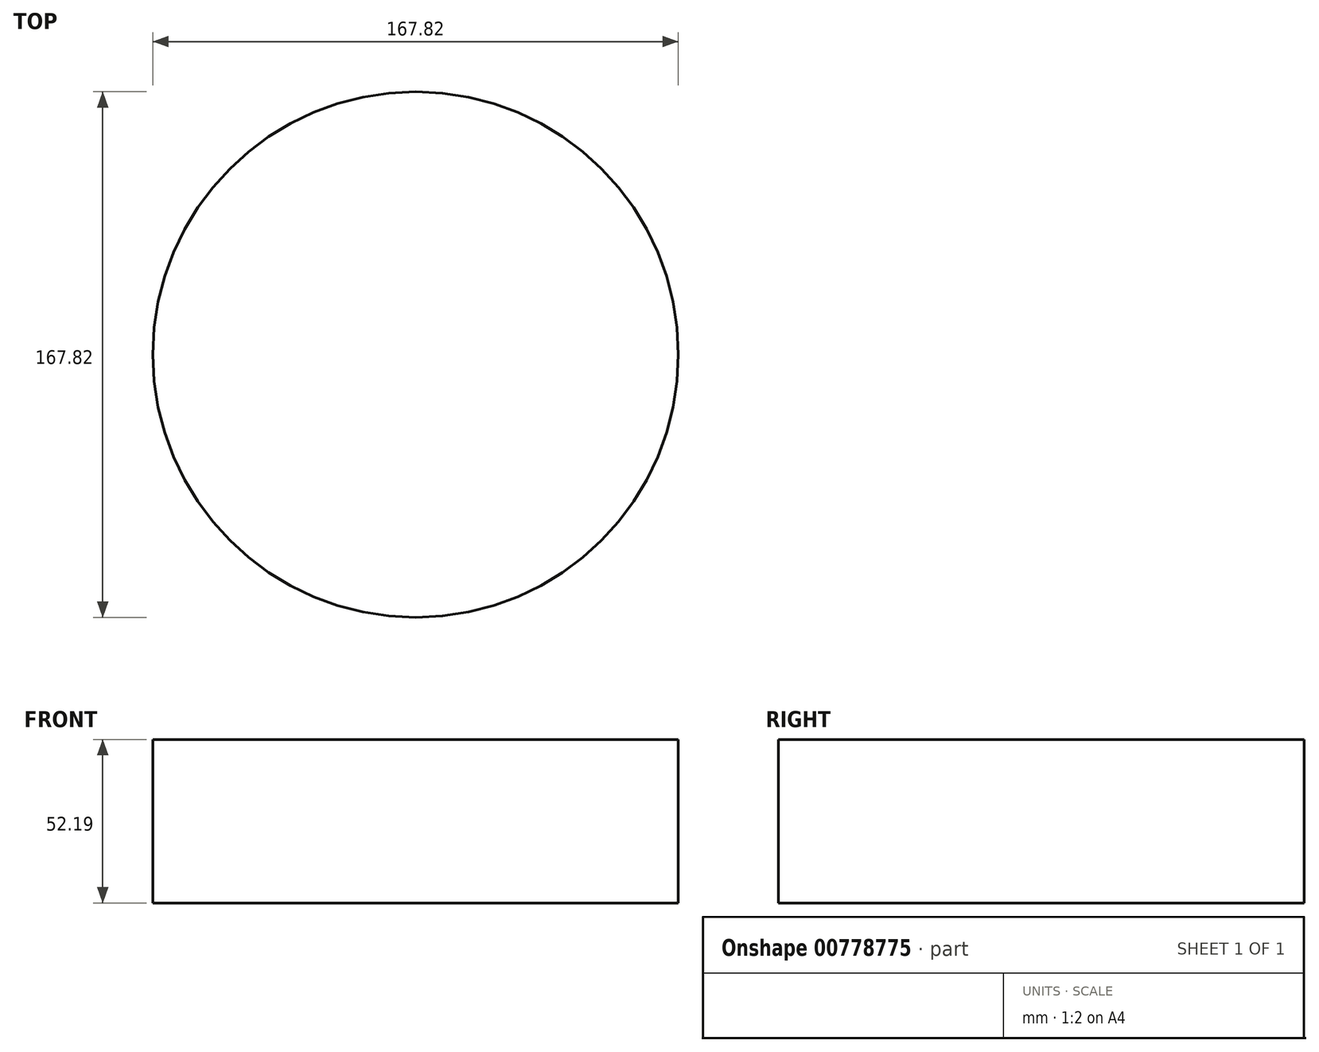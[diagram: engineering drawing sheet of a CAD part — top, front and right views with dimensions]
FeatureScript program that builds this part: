
annotation { "Feature Type Name" : "Feature", "Feature Type Description" : "" }
export const myFeature = defineFeature(function(context is Context, id is Id, definition is map)
    precondition{}
    {
        {
            var Q0;
            Q0=qCreatedBy(makeId("Front.planeOp"),FACE);
            var sketch = newSketch(context, id + "F0", { "sketchPlane" : qUnion([Q0])});
            skLineSegment(sketch, "E0.bottom", {"start": v(-36, 26.81) * mm, "end": v(47.9, 26.81) * mm});
            skLineSegment(sketch, "E0.top", {"start": v(-36, -25.38) * mm, "end": v(47.9, -25.38) * mm});
            skLineSegment(sketch, "E0.left", {"start": v(-36, 26.81) * mm, "end": v(-36, -25.38) * mm});
            skLineSegment(sketch, "E0.right", {"start": v(47.9, 26.81) * mm, "end": v(47.9, -25.38) * mm});
            skSolve(sketch);
        }
        {
            var Q0;
            Q0=makeQuery(id+"F0.imprint","IMPRINT",FACE,{"disambiguationData":[TD([[makeQuery(id+"F0.imprint","IMPRINT",EDGE,{"derivedFrom":sQuery(id+"F0.wireOp",EDGE,"E0.bottom")}),-1.0]])]});
            var Q1;
            Q1=sQuery(id+"F0.wireOp",EDGE,"E0.right");
            revolve(context, id + "F1", {"surfaceOperationType" : NewSurfaceOperationType.NEW, "entities" : qUnion([Q0]), "axis" : qUnion([Q1]), "revolveType" : RevolveType.FULL});
        }
    });
